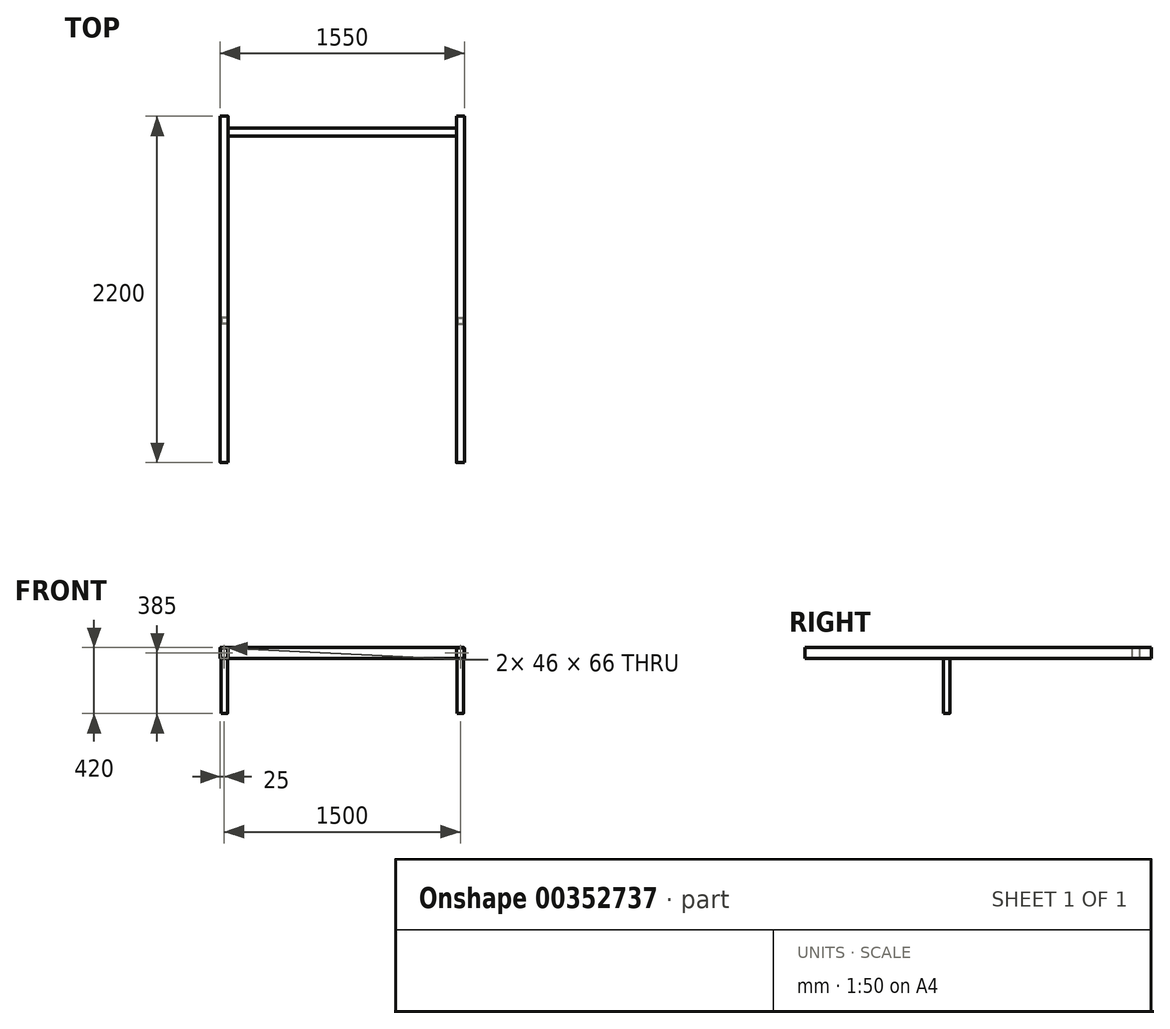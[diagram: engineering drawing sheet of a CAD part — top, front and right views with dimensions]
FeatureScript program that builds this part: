
annotation { "Feature Type Name" : "Feature", "Feature Type Description" : "" }
export const myFeature = defineFeature(function(context is Context, id is Id, definition is map)
    precondition{}
    {
        {
            var Q0;
            Q0=qCreatedBy(makeId("Front.planeOp"),FACE);
            var sketch = newSketch(context, id + "F0", { "sketchPlane" : qUnion([Q0])});
            skLineSegment(sketch, "E0.bottom", {"start": v(772.46, 835) * mm, "end": v(727.54, 835) * mm});
            skLineSegment(sketch, "E0.top", {"start": v(772.46, 765) * mm, "end": v(727.54, 765) * mm});
            skLineSegment(sketch, "E0.left", {"start": v(775, 832.46) * mm, "end": v(775, 767.54) * mm});
            skLineSegment(sketch, "E0.right", {"start": v(725, 832.46) * mm, "end": v(725, 767.54) * mm});
            skPoint(sketch, "E0.middle", {"position": v(750, 800) * mm});
            skPoint(sketch, "E1.visualSharp", {"position": v(725, 835) * mm});
            skArc(sketch, "E1.filletArc", {"start": v(727.54, 835) * mm, "mid": v(725.74, 834.26) * mm, "end": v(725, 832.46) * mm});
            skPoint(sketch, "E2.visualSharp", {"position": v(775, 835) * mm});
            skArc(sketch, "E2.filletArc", {"start": v(775, 832.46) * mm, "mid": v(774.26, 834.26) * mm, "end": v(772.46, 835) * mm});
            skPoint(sketch, "E3.visualSharp", {"position": v(775, 765) * mm});
            skArc(sketch, "E3.filletArc", {"start": v(772.46, 765) * mm, "mid": v(774.26, 765.74) * mm, "end": v(775, 767.54) * mm});
            skPoint(sketch, "E4.visualSharp", {"position": v(725, 765) * mm});
            skArc(sketch, "E4.filletArc", {"start": v(725, 767.54) * mm, "mid": v(725.74, 765.74) * mm, "end": v(727.54, 765) * mm});
            skLineSegment(sketch, "E5.0", {"start": v(773, 833) * mm, "end": v(727, 833) * mm});
            skLineSegment(sketch, "E5.1", {"start": v(773, 833) * mm, "end": v(773, 767) * mm});
            skLineSegment(sketch, "E5.2", {"start": v(773, 767) * mm, "end": v(727, 767) * mm});
            skLineSegment(sketch, "E5.3", {"start": v(727, 833) * mm, "end": v(727, 767) * mm});
            skArc(sketch, "E6.MirrorCS", {"start": v(-725, 767.54) * mm, "mid": v(-725.74, 765.74) * mm, "end": v(-727.54, 765) * mm});
            skArc(sketch, "E7.MirrorCS", {"start": v(-727.54, 835) * mm, "mid": v(-725.74, 834.26) * mm, "end": v(-725, 832.46) * mm});
            skLineSegment(sketch, "E8.MirrorCS", {"start": v(-773, 767) * mm, "end": v(-727, 767) * mm});
            skLineSegment(sketch, "E9.MirrorCS", {"start": v(-772.46, 765) * mm, "end": v(-727.54, 765) * mm});
            skArc(sketch, "E10.MirrorCS", {"start": v(-772.46, 765) * mm, "mid": v(-774.26, 765.74) * mm, "end": v(-775, 767.54) * mm});
            skArc(sketch, "E11.MirrorCS", {"start": v(-775, 832.46) * mm, "mid": v(-774.26, 834.26) * mm, "end": v(-772.46, 835) * mm});
            skLineSegment(sketch, "E12.MirrorCS", {"start": v(-773, 833) * mm, "end": v(-727, 833) * mm});
            skLineSegment(sketch, "E13.MirrorCS", {"start": v(-772.46, 835) * mm, "end": v(-727.54, 835) * mm});
            skLineSegment(sketch, "E14.MirrorCS", {"start": v(-725, 832.46) * mm, "end": v(-725, 767.54) * mm});
            skLineSegment(sketch, "E15.MirrorCS", {"start": v(-727, 833) * mm, "end": v(-727, 767) * mm});
            skLineSegment(sketch, "E16.MirrorCS", {"start": v(-775, 832.46) * mm, "end": v(-775, 767.54) * mm});
            skLineSegment(sketch, "E17.MirrorCS", {"start": v(-773, 833) * mm, "end": v(-773, 767) * mm});
            skPoint(sketch, "E18.MirrorP", {"position": v(-775, 835) * mm});
            skPoint(sketch, "E19.MirrorP", {"position": v(-725, 835) * mm});
            skPoint(sketch, "E20.MirrorP", {"position": v(-725, 765) * mm});
            skPoint(sketch, "E21.MirrorP", {"position": v(-775, 765) * mm});
            skPoint(sketch, "E22.MirrorP", {"position": v(-750, 800) * mm});
            skSolve(sketch);
        }
        {
            var Q0;
            Q0 = qSketchRegion(id + "F0", true);
            extrude(context, id + "F1", {"entities" : qUnion([Q0]), "endBound" : BoundingType.SYMMETRIC, "depth" : 2200 * mm});
        }
        {
            var Q0;
            Q0=qCreatedBy(makeId("Right.planeOp"),FACE);
            var sketch = newSketch(context, id + "F2", { "sketchPlane" : qUnion([Q0])});
            skLineSegment(sketch, "E23.bottom", {"start": v(1022.46, 835) * mm, "end": v(977.54, 835) * mm});
            skLineSegment(sketch, "E23.top", {"start": v(1022.46, 765) * mm, "end": v(977.54, 765) * mm});
            skLineSegment(sketch, "E23.left", {"start": v(1025, 832.46) * mm, "end": v(1025, 767.54) * mm});
            skLineSegment(sketch, "E23.right", {"start": v(975, 832.46) * mm, "end": v(975, 767.54) * mm});
            skPoint(sketch, "E23.middle", {"position": v(1000, 800) * mm});
            skPoint(sketch, "E24.visualSharp", {"position": v(975, 835) * mm});
            skArc(sketch, "E24.filletArc", {"start": v(977.54, 835) * mm, "mid": v(975.74, 834.26) * mm, "end": v(975, 832.46) * mm});
            skPoint(sketch, "E25.visualSharp", {"position": v(1025, 835) * mm});
            skArc(sketch, "E25.filletArc", {"start": v(1025, 832.46) * mm, "mid": v(1024.26, 834.26) * mm, "end": v(1022.46, 835) * mm});
            skPoint(sketch, "E26.visualSharp", {"position": v(1025, 765) * mm});
            skArc(sketch, "E26.filletArc", {"start": v(1022.46, 765) * mm, "mid": v(1024.26, 765.74) * mm, "end": v(1025, 767.54) * mm});
            skPoint(sketch, "E27.visualSharp", {"position": v(975, 765) * mm});
            skArc(sketch, "E27.filletArc", {"start": v(975, 767.54) * mm, "mid": v(975.74, 765.74) * mm, "end": v(977.54, 765) * mm});
            skLineSegment(sketch, "E28.0", {"start": v(977, 833) * mm, "end": v(977, 767) * mm});
            skLineSegment(sketch, "E28.1", {"start": v(1023, 833) * mm, "end": v(977, 833) * mm});
            skLineSegment(sketch, "E28.2", {"start": v(1023, 833) * mm, "end": v(1023, 767) * mm});
            skLineSegment(sketch, "E28.3", {"start": v(1023, 767) * mm, "end": v(977, 767) * mm});
            skSolve(sketch);
        }
        {
            var Q0;
            Q0 = qSketchRegion(id + "F2", true);
            extrude(context, id + "F3", {"entities" : qUnion([Q0]), "operationType" : NewBodyOperationType.ADD, "endBound" : BoundingType.SYMMETRIC, "depth" : 1450 * mm});
        }
        {
            var Q0;
            Q0=qCreatedBy(makeId("Top.planeOp"),FACE);
            cPlane(context, id + "F4", {"entities" : qUnion([Q0]), "cplaneType" : CPlaneType.OFFSET, "offset" : 765 * mm, "width" : 152.4 * mm, "height" : 152.4 * mm});
        }
        {
            var Q0;
            Q0=qCreatedBy(id+"F4.planeOp",FACE);
            var sketch = newSketch(context, id + "F5", { "sketchPlane" : qUnion([Q0])});
            skLineSegment(sketch, "E29.bottom", {"start": v(732.54, -180) * mm, "end": v(767.46, -180) * mm});
            skLineSegment(sketch, "E29.top", {"start": v(732.54, -220) * mm, "end": v(767.46, -220) * mm});
            skLineSegment(sketch, "E29.left", {"start": v(730, -182.54) * mm, "end": v(730, -217.46) * mm});
            skLineSegment(sketch, "E29.right", {"start": v(770, -182.54) * mm, "end": v(770, -217.46) * mm});
            skPoint(sketch, "E29.middle", {"position": v(750, -200) * mm});
            skPoint(sketch, "E30.visualSharp", {"position": v(730, -180) * mm});
            skArc(sketch, "E30.filletArc", {"start": v(732.54, -180) * mm, "mid": v(730.74, -180.74) * mm, "end": v(730, -182.54) * mm});
            skPoint(sketch, "E31.visualSharp", {"position": v(770, -180) * mm});
            skArc(sketch, "E31.filletArc", {"start": v(770, -182.54) * mm, "mid": v(769.26, -180.74) * mm, "end": v(767.46, -180) * mm});
            skPoint(sketch, "E32.visualSharp", {"position": v(770, -220) * mm});
            skArc(sketch, "E32.filletArc", {"start": v(767.46, -220) * mm, "mid": v(769.26, -219.26) * mm, "end": v(770, -217.46) * mm});
            skPoint(sketch, "E33.visualSharp", {"position": v(730, -220) * mm});
            skArc(sketch, "E33.filletArc", {"start": v(730, -217.46) * mm, "mid": v(730.74, -219.26) * mm, "end": v(732.54, -220) * mm});
            skLineSegment(sketch, "E34.0", {"start": v(732, -182) * mm, "end": v(732, -218) * mm});
            skLineSegment(sketch, "E34.1", {"start": v(732, -182) * mm, "end": v(768, -182) * mm});
            skLineSegment(sketch, "E34.2", {"start": v(768, -182) * mm, "end": v(768, -218) * mm});
            skLineSegment(sketch, "E34.3", {"start": v(732, -218) * mm, "end": v(768, -218) * mm});
            skArc(sketch, "E35.MirrorCS", {"start": v(-732.54, -180) * mm, "mid": v(-730.74, -180.74) * mm, "end": v(-730, -182.54) * mm});
            skArc(sketch, "E36.MirrorCS", {"start": v(-770, -182.54) * mm, "mid": v(-769.26, -180.74) * mm, "end": v(-767.46, -180) * mm});
            skArc(sketch, "E37.MirrorCS", {"start": v(-730, -217.46) * mm, "mid": v(-730.74, -219.26) * mm, "end": v(-732.54, -220) * mm});
            skArc(sketch, "E38.MirrorCS", {"start": v(-767.46, -220) * mm, "mid": v(-769.26, -219.26) * mm, "end": v(-770, -217.46) * mm});
            skLineSegment(sketch, "E39.MirrorCS", {"start": v(-732.54, -180) * mm, "end": v(-767.46, -180) * mm});
            skLineSegment(sketch, "E40.MirrorCS", {"start": v(-770, -182.54) * mm, "end": v(-770, -217.46) * mm});
            skLineSegment(sketch, "E41.MirrorCS", {"start": v(-730, -182.54) * mm, "end": v(-730, -217.46) * mm});
            skLineSegment(sketch, "E42.MirrorCS", {"start": v(-732, -182) * mm, "end": v(-732, -218) * mm});
            skLineSegment(sketch, "E43.MirrorCS", {"start": v(-768, -182) * mm, "end": v(-768, -218) * mm});
            skLineSegment(sketch, "E44.MirrorCS", {"start": v(-732, -182) * mm, "end": v(-768, -182) * mm});
            skPoint(sketch, "E45.MirrorP", {"position": v(-730, -180) * mm});
            skPoint(sketch, "E46.MirrorP", {"position": v(-770, -180) * mm});
            skPoint(sketch, "E47.MirrorP", {"position": v(-750, -200) * mm});
            skLineSegment(sketch, "E48.MirrorCS", {"start": v(-732.54, -220) * mm, "end": v(-767.46, -220) * mm});
            skLineSegment(sketch, "E49.MirrorCS", {"start": v(-732, -218) * mm, "end": v(-768, -218) * mm});
            skPoint(sketch, "E50.MirrorP", {"position": v(-730, -220) * mm});
            skPoint(sketch, "E51.MirrorP", {"position": v(-770, -220) * mm});
            skSolve(sketch);
        }
        {
            var Q0;
            Q0 = qSketchRegion(id + "F5", true);
            extrude(context, id + "F6", {"entities" : qUnion([Q0]), "operationType" : NewBodyOperationType.ADD, "oppositeDirection" : true, "depth" : 350 * mm});
        }
    });
